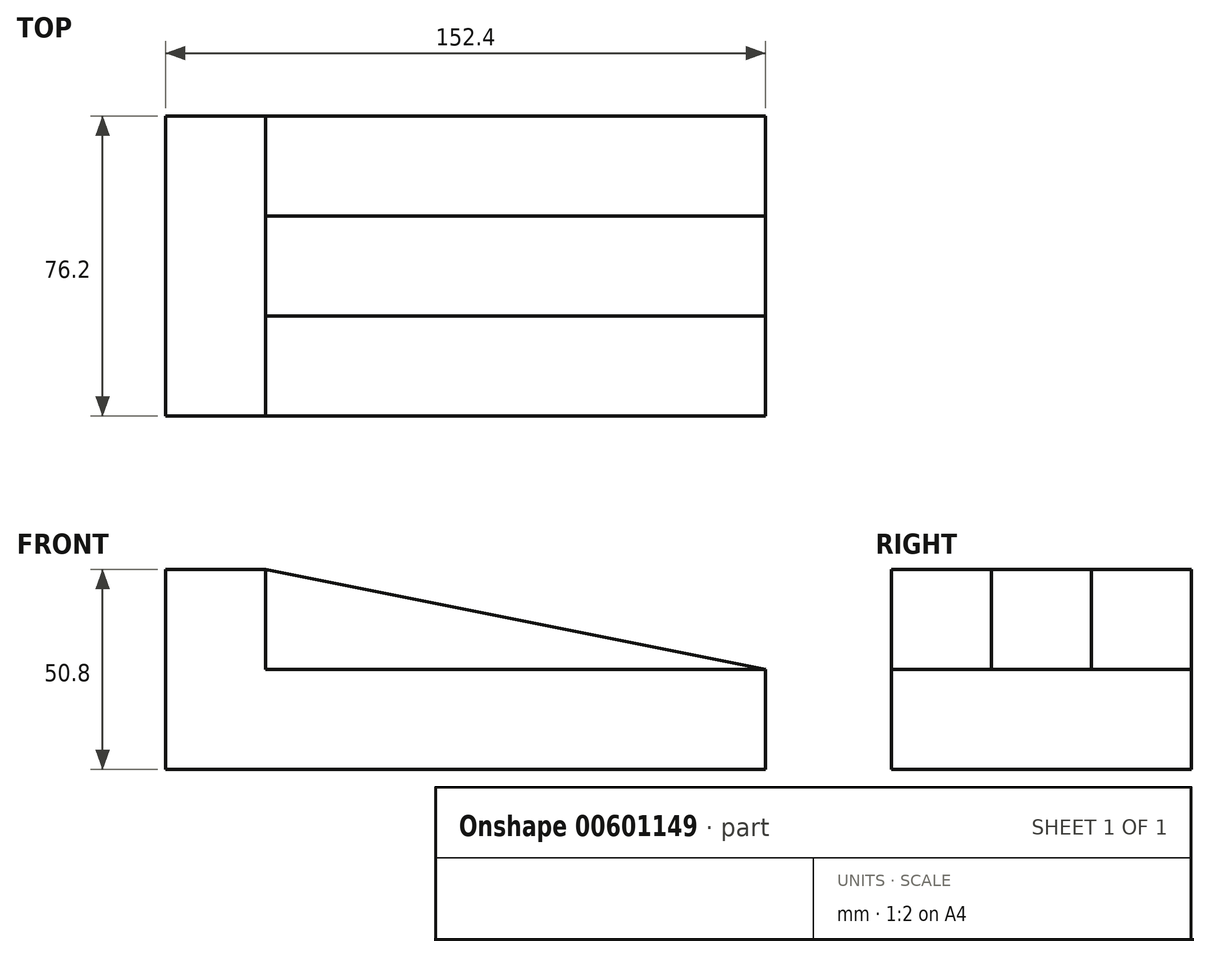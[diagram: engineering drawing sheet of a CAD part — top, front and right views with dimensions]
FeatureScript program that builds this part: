
annotation { "Feature Type Name" : "Feature", "Feature Type Description" : "" }
export const myFeature = defineFeature(function(context is Context, id is Id, definition is map)
    precondition{}
    {
        {
            var Q0;
            Q0=qCreatedBy(makeId("Front.planeOp"),FACE);
            var sketch = newSketch(context, id + "F0", { "sketchPlane" : qUnion([Q0])});
            skLineSegment(sketch, "E0", {"start": v(0, 0) * mm, "end": v(0, 50.8) * mm});
            skLineSegment(sketch, "E1", {"start": v(0, 0) * mm, "end": v(152.4, 0) * mm});
            skLineSegment(sketch, "E2", {"start": v(0, 50.8) * mm, "end": v(25.4, 50.8) * mm});
            skLineSegment(sketch, "E3", {"start": v(152.4, 0) * mm, "end": v(152.4, 25.4) * mm});
            skLineSegment(sketch, "E4", {"start": v(25.4, 50.8) * mm, "end": v(152.4, 25.4) * mm});
            skSolve(sketch);
        }
        {
            var Q0;
            Q0=makeQuery(id+"F0.imprint","IMPRINT",FACE,{"disambiguationData":[TD([[makeQuery(id+"F0.imprint","IMPRINT",EDGE,{"derivedFrom":sQuery(id+"F0.wireOp",EDGE,"E0")}),-1.0]])]});
            extrude(context, id + "F1", {"entities" : qUnion([Q0]), "depth" : 76.2 * mm, "offsetDistance" : 25.4 * mm});
        }
        {
            var Q0;
            Q0=makeQuery(id+"F1.opExtrude","CAP_FACE",FACE,{"disambiguationData":[OSD([sQuery(id+"F0.wireOp",EDGE,"E0"),sQuery(id+"F0.wireOp",EDGE,"E1"),sQuery(id+"F0.wireOp",EDGE,"E2"),sQuery(id+"F0.wireOp",EDGE,"E3"),sQuery(id+"F0.wireOp",EDGE,"E4")])],"isStart":false});
            var sketch = newSketch(context, id + "F2", { "sketchPlane" : qUnion([Q0])});
            skLineSegment(sketch, "E5", {"start": v(25.4, 50.8) * mm, "end": v(25.4, 25.4) * mm});
            skLineSegment(sketch, "E6", {"start": v(25.4, 25.4) * mm, "end": v(152.4, 25.4) * mm});
            skSolve(sketch);
        }
        {
            var Q0;
            Q0 = qSketchRegion(id + "F2", true);
            var Q1;
            Q1=makeQuery(id+"F2.imprint","IMPRINT",FACE,{"disambiguationData":[TD([[makeQuery(id+"F2.imprint","IMPRINT",EDGE,{"derivedFrom":sQuery(id+"F2.wireOp",EDGE,"E5")}),1.0]])]});
            extrude(context, id + "F3", {"entities" : qUnion([Q0, Q1]), "operationType" : NewBodyOperationType.REMOVE, "oppositeDirection" : true, "depth" : 25.4 * mm, "offsetDistance" : 25.4 * mm});
        }
        {
            var Q0;
            Q0=makeQuery(id+"F1.opExtrude","CAP_FACE",FACE,{"disambiguationData":[OSD([sQuery(id+"F0.wireOp",EDGE,"E0"),sQuery(id+"F0.wireOp",EDGE,"E1"),sQuery(id+"F0.wireOp",EDGE,"E2"),sQuery(id+"F0.wireOp",EDGE,"E3"),sQuery(id+"F0.wireOp",EDGE,"E4")])],"isStart":true});
            var sketch = newSketch(context, id + "F4", { "sketchPlane" : qUnion([Q0])});
            skLineSegment(sketch, "E7", {"start": v(-25.4, 50.8) * mm, "end": v(-25.4, 25.4) * mm});
            skLineSegment(sketch, "E8", {"start": v(-25.4, 25.4) * mm, "end": v(-152.4, 25.4) * mm});
            skSolve(sketch);
        }
        {
            var Q0;
            Q0 = qSketchRegion(id + "F4", true);
            var Q1;
            Q1=makeQuery(id+"F4.imprint","IMPRINT",FACE,{"disambiguationData":[TD([[makeQuery(id+"F4.imprint","IMPRINT",EDGE,{"derivedFrom":sQuery(id+"F4.wireOp",EDGE,"E7")}),-1.0]])]});
            extrude(context, id + "F5", {"entities" : qUnion([Q0, Q1]), "operationType" : NewBodyOperationType.REMOVE, "oppositeDirection" : true, "depth" : 25.4 * mm, "offsetDistance" : 25.4 * mm});
        }
    });
